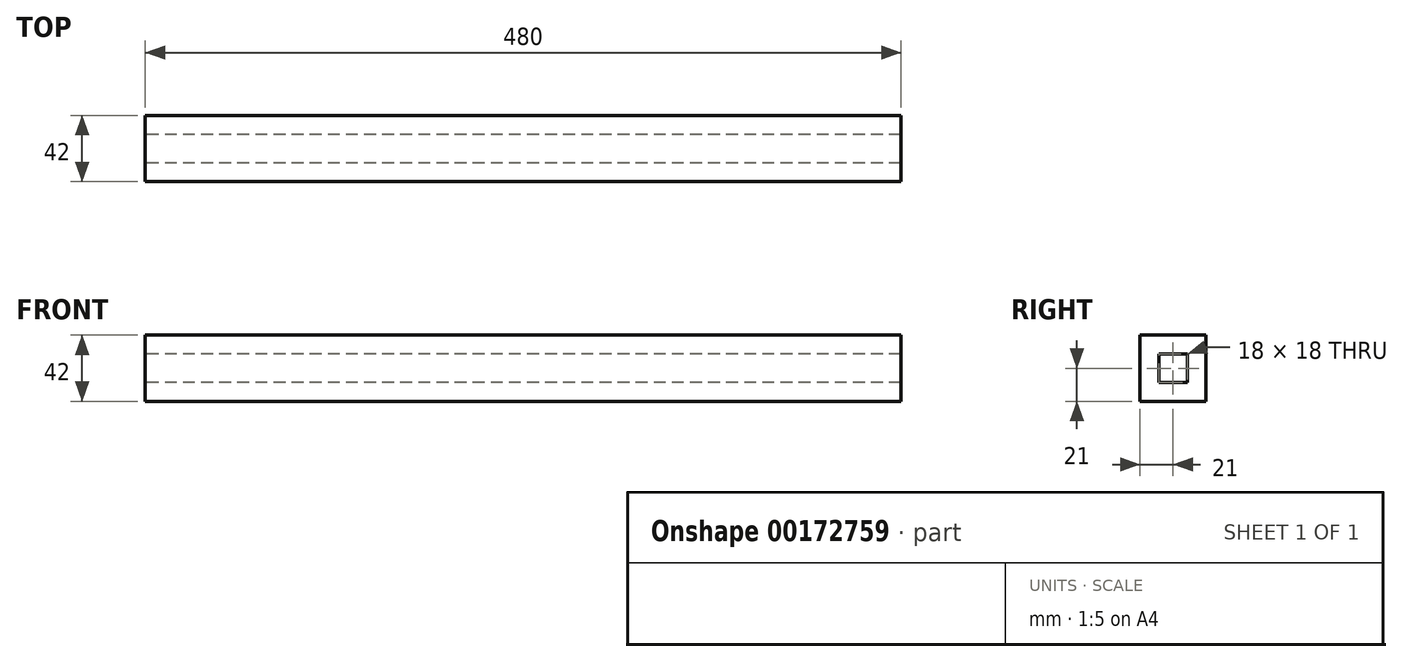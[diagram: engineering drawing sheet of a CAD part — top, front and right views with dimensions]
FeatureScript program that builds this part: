
annotation { "Feature Type Name" : "Feature", "Feature Type Description" : "" }
export const myFeature = defineFeature(function(context is Context, id is Id, definition is map)
    precondition{}
    {
        {
            var Q0;
            Q0=qCreatedBy(makeId("Right.planeOp"),FACE);
            var sketch = newSketch(context, id + "F0", { "sketchPlane" : qUnion([Q0])});
            skLineSegment(sketch, "E0.0", {"start": v(9, -9) * mm, "end": v(-9, -9) * mm, "construction": true});
            skLineSegment(sketch, "E0.1", {"start": v(-9, -9) * mm, "end": v(-9, 9) * mm, "construction": true});
            skLineSegment(sketch, "E0.2", {"start": v(-9, 9) * mm, "end": v(9, 9) * mm, "construction": true});
            skLineSegment(sketch, "E0.3", {"start": v(9, 9) * mm, "end": v(9, -9) * mm, "construction": true});
            skPoint(sketch, "E0.0.midPoint", {"position": v(0, -9) * mm});
            skLineSegment(sketch, "E1.0", {"start": v(-21, 21) * mm, "end": v(21, 21) * mm, "construction": true});
            skLineSegment(sketch, "E1.1", {"start": v(-21, -21) * mm, "end": v(-21, 21) * mm, "construction": true});
            skLineSegment(sketch, "E1.2", {"start": v(21, -21) * mm, "end": v(-21, -21) * mm, "construction": true});
            skLineSegment(sketch, "E1.3", {"start": v(21, 21) * mm, "end": v(21, -21) * mm, "construction": true});
            skLineSegment(sketch, "E2", {"start": v(-21, 21) * mm, "end": v(-21, -21) * mm});
            skLineSegment(sketch, "E3", {"start": v(21, -21) * mm, "end": v(21, 21) * mm});
            skLineSegment(sketch, "E4", {"start": v(21, 21) * mm, "end": v(-21, 21) * mm});
            skLineSegment(sketch, "E5", {"start": v(-21, -21) * mm, "end": v(21, -21) * mm});
            skLineSegment(sketch, "E6", {"start": v(9, -9) * mm, "end": v(-9, -9) * mm});
            skLineSegment(sketch, "E7", {"start": v(-9, -9) * mm, "end": v(-9, 9) * mm});
            skLineSegment(sketch, "E8", {"start": v(-9, 9) * mm, "end": v(9, 9) * mm});
            skLineSegment(sketch, "E9", {"start": v(9, 9) * mm, "end": v(9, -9) * mm});
            skSolve(sketch);
        }
        {
            var Q0;
            Q0=makeQuery(id+"F0.imprint","IMPRINT",FACE,{"disambiguationData":[TD([[makeQuery(id+"F0.imprint","IMPRINT",EDGE,{"derivedFrom":sQuery(id+"F0.wireOp",EDGE,"E2")}),1.0]])]});
            extrude(context, id + "F1", {"entities" : qUnion([Q0]), "depth" : 480 * mm});
        }
    });
